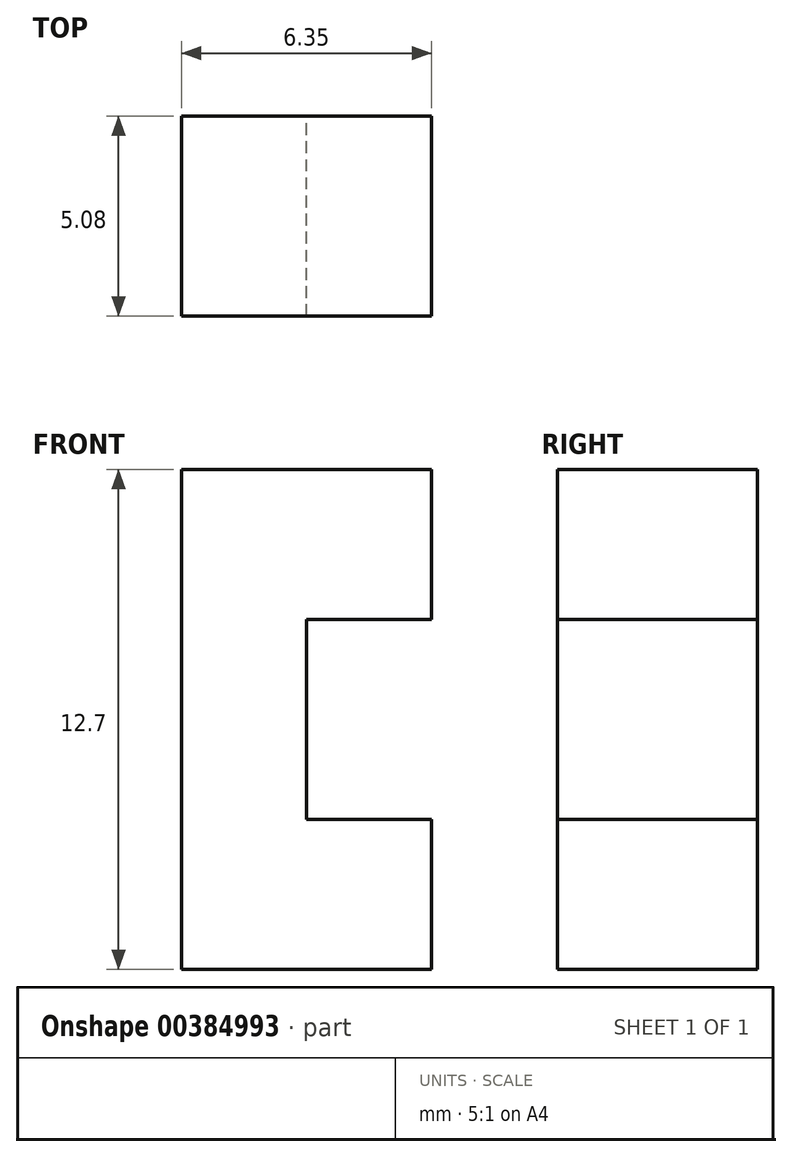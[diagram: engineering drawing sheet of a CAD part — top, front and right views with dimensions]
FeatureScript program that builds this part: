
annotation { "Feature Type Name" : "Feature", "Feature Type Description" : "" }
export const myFeature = defineFeature(function(context is Context, id is Id, definition is map)
    precondition{}
    {
        {
            var Q0;
            Q0=qCreatedBy(makeId("Front.planeOp"),FACE);
            var sketch = newSketch(context, id + "F0", { "sketchPlane" : qUnion([Q0])});
            skLineSegment(sketch, "E0.bottom", {"start": v(-6.35, 12.7) * mm, "end": v(0, 12.7) * mm});
            skLineSegment(sketch, "E0.top", {"start": v(-6.35, 0) * mm, "end": v(0, 0) * mm});
            skLineSegment(sketch, "E0.left", {"start": v(-6.35, 12.7) * mm, "end": v(-6.35, 0) * mm});
            skLineSegment(sketch, "E0.right", {"start": v(0, 12.7) * mm, "end": v(0, 0) * mm});
            skSolve(sketch);
        }
        {
            var Q0;
            Q0=makeQuery(id+"F0.imprint","IMPRINT",FACE,{"disambiguationData":[TD([[makeQuery(id+"F0.imprint","IMPRINT",EDGE,{"derivedFrom":sQuery(id+"F0.wireOp",EDGE,"E0.bottom")}),-1.0]])]});
            extrude(context, id + "F1", {"entities" : qUnion([Q0]), "depth" : 5.08 * mm, "offsetDistance" : 25.4 * mm});
        }
        {
            var Q0;
            Q0=makeQuery(id+"F1.opExtrude","SWEPT_FACE",FACE,{"disambiguationData":[OSD([sQuery(id+"F0.wireOp",EDGE,"E0.right")])]});
            var sketch = newSketch(context, id + "F2", { "sketchPlane" : qUnion([Q0])});
            skLineSegment(sketch, "E1.bottom", {"start": v(-5.08, 8.9) * mm, "end": v(0, 8.9) * mm});
            skLineSegment(sketch, "E1.top", {"start": v(-5.08, 3.81) * mm, "end": v(0, 3.81) * mm});
            skLineSegment(sketch, "E1.left", {"start": v(-5.08, 8.9) * mm, "end": v(-5.08, 3.81) * mm});
            skLineSegment(sketch, "E1.right", {"start": v(0, 8.9) * mm, "end": v(0, 3.81) * mm});
            skSolve(sketch);
        }
        {
            var Q0;
            Q0=makeQuery(id+"F2.imprint","IMPRINT",FACE,{"disambiguationData":[TD([[makeQuery(id+"F2.imprint","IMPRINT",EDGE,{"derivedFrom":sQuery(id+"F2.wireOp",EDGE,"E1.bottom")}),-1.0]])]});
            extrude(context, id + "F3", {"entities" : qUnion([Q0]), "operationType" : NewBodyOperationType.REMOVE, "oppositeDirection" : true, "depth" : 3.17 * mm, "offsetDistance" : 25.4 * mm});
        }
    });
